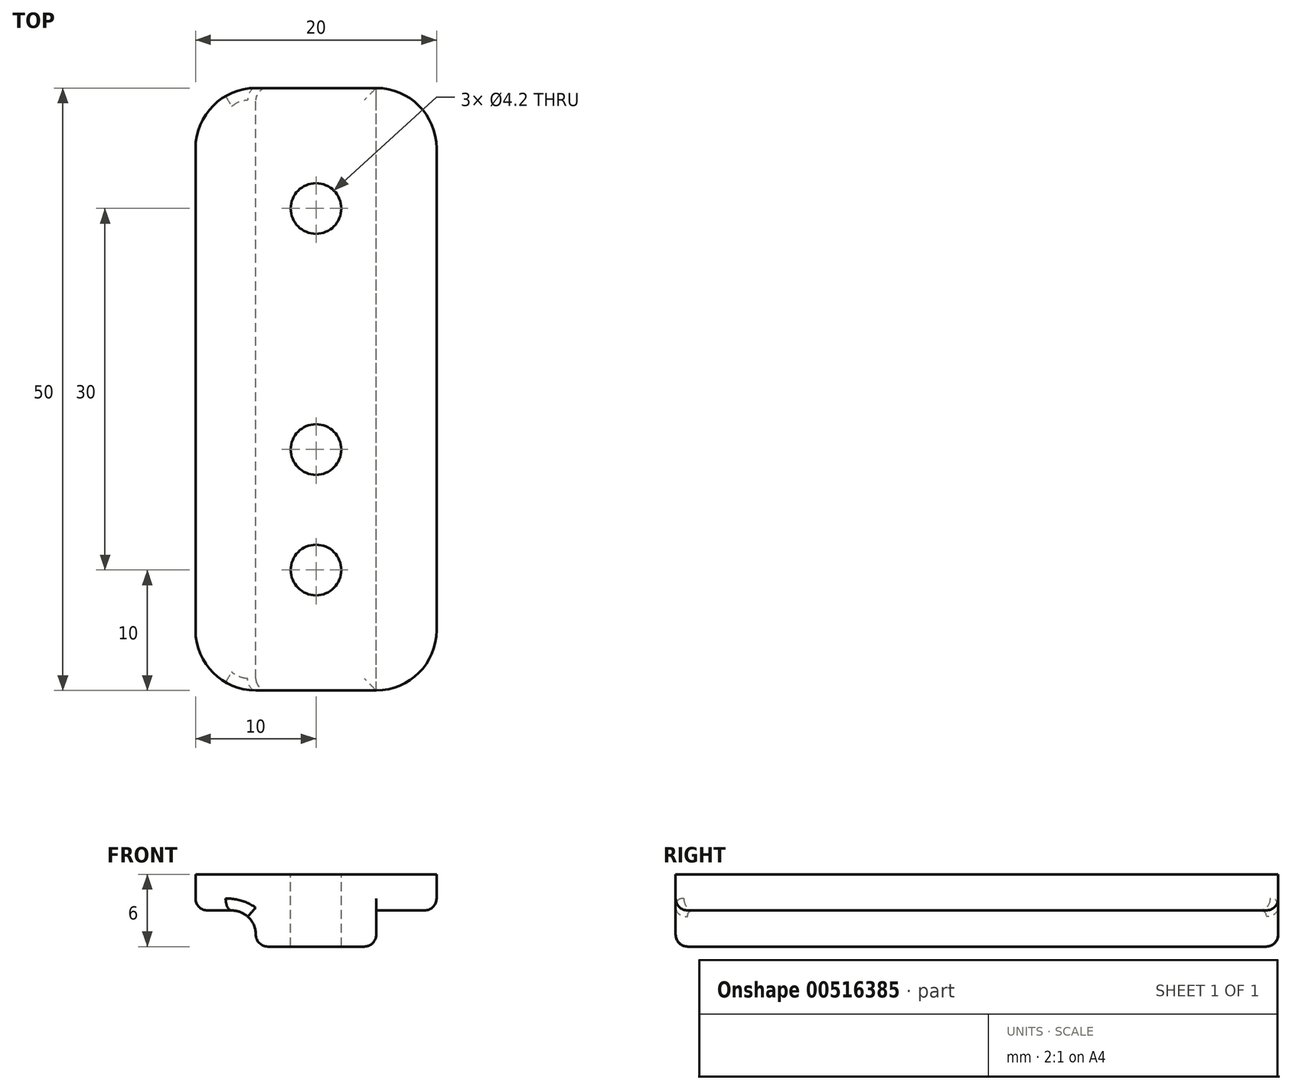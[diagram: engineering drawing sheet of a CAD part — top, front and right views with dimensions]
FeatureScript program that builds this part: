
annotation { "Feature Type Name" : "Feature", "Feature Type Description" : "" }
export const myFeature = defineFeature(function(context is Context, id is Id, definition is map)
    precondition{}
    {
        {
            var Q0;
            Q0=qCreatedBy(makeId("Top.planeOp"),FACE);
            var sketch = newSketch(context, id + "F0", { "sketchPlane" : qUnion([Q0])});
            skLineSegment(sketch, "E0.bottom", {"start": v(-10, 25) * mm, "end": v(10, 25) * mm});
            skLineSegment(sketch, "E0.top", {"start": v(-10, -25) * mm, "end": v(10, -25) * mm});
            skLineSegment(sketch, "E0.left", {"start": v(-10, 25) * mm, "end": v(-10, -25) * mm});
            skLineSegment(sketch, "E0.right", {"start": v(10, 25) * mm, "end": v(10, -25) * mm});
            skSolve(sketch);
        }
        {
            var Q0;
            Q0 = qSketchRegion(id + "F0", true);
            extrude(context, id + "F1", {"entities" : qUnion([Q0]), "depth" : 3 * mm, "offsetDistance" : 25 * mm});
        }
        {
            var Q0;
            Q0=makeQuery(id+"F1.opExtrude","CAP_FACE",FACE,{"disambiguationData":[OSD([sQuery(id+"F0.wireOp",EDGE,"E0.bottom"),sQuery(id+"F0.wireOp",EDGE,"E0.top"),sQuery(id+"F0.wireOp",EDGE,"E0.left"),sQuery(id+"F0.wireOp",EDGE,"E0.right")])],"isStart":false});
            var sketch = newSketch(context, id + "F2", { "sketchPlane" : qUnion([Q0])});
            skCircle(sketch, "E1", {"center": v(0, 15) * mm, "radius": 2.1 * mm});
            skCircle(sketch, "E2", {"center": v(0, -5) * mm, "radius": 2.1 * mm});
            skCircle(sketch, "E3", {"center": v(0, -15) * mm, "radius": 2.1 * mm});
            skSolve(sketch);
        }
        {
            var Q0;
            Q0 = qSketchRegion(id + "F2", true);
            extrude(context, id + "F3", {"entities" : qUnion([Q0]), "operationType" : NewBodyOperationType.REMOVE, "endBound" : BoundingType.THROUGH_ALL, "oppositeDirection" : true, "depth" : 25 * mm, "offsetDistance" : 25 * mm});
        }
        {
            var Q0;
            Q0=makeQuery(id+"F1.opExtrude","SWEPT_EDGE",EDGE,{"disambiguationData":[OSD([sQuery(id+"F0.wireOp",EDGE,"E0.top"),sQuery(id+"F0.wireOp",EDGE,"E0.right")])]});
            var Q1;
            Q1=makeQuery(id+"F1.opExtrude","SWEPT_EDGE",EDGE,{"disambiguationData":[OSD([sQuery(id+"F0.wireOp",EDGE,"E0.top"),sQuery(id+"F0.wireOp",EDGE,"E0.left")])]});
            var Q2;
            Q2=makeQuery(id+"F1.opExtrude","SWEPT_EDGE",EDGE,{"disambiguationData":[OSD([sQuery(id+"F0.wireOp",EDGE,"E0.bottom"),sQuery(id+"F0.wireOp",EDGE,"E0.right")])]});
            var Q3;
            Q3=makeQuery(id+"F1.opExtrude","SWEPT_EDGE",EDGE,{"disambiguationData":[OSD([sQuery(id+"F0.wireOp",EDGE,"E0.bottom"),sQuery(id+"F0.wireOp",EDGE,"E0.left")])]});
            fillet(context, id + "F4", {"entities" : qUnion([Q0, Q1, Q2, Q3]), "radius" : 5 * mm, "tangentPropagation" : true, "allowEdgeOverflow" : false});
        }
        {
            var Q0;
            Q0=makeQuery(id+"F1.opExtrude","CAP_FACE",FACE,{"disambiguationData":[OSD([sQuery(id+"F0.wireOp",EDGE,"E0.bottom"),sQuery(id+"F0.wireOp",EDGE,"E0.top"),sQuery(id+"F0.wireOp",EDGE,"E0.left"),sQuery(id+"F0.wireOp",EDGE,"E0.right")])],"isStart":true});
            var sketch = newSketch(context, id + "F5", { "sketchPlane" : qUnion([Q0])});
            skLineSegment(sketch, "E4.bottom", {"start": v(-5, 25) * mm, "end": v(5, 25) * mm});
            skLineSegment(sketch, "E4.top", {"start": v(-5, -25) * mm, "end": v(5, -25) * mm});
            skLineSegment(sketch, "E4.left", {"start": v(-5, 25) * mm, "end": v(-5, -25) * mm});
            skLineSegment(sketch, "E4.right", {"start": v(5, 25) * mm, "end": v(5, -25) * mm});
            skSolve(sketch);
        }
        {
            var Q0;
            Q0=makeQuery(id+"F5.imprint","IMPRINT",FACE,{"disambiguationData":[TD([[makeQuery(id+"F5.imprint","IMPRINT",EDGE,{"derivedFrom":sQuery(id+"F5.wireOp",EDGE,"E4.bottom")}),-1.0]])]});
            extrude(context, id + "F6", {"entities" : qUnion([Q0]), "operationType" : NewBodyOperationType.ADD, "depth" : 3 * mm, "offsetDistance" : 25 * mm});
        }
        {
            var Q0;
            Q0=makeQuery(id+"F6.opExtrude","CAP_EDGE",EDGE,{"disambiguationData":[OSD([sQuery(id+"F5.wireOp",EDGE,"E4.left")])],"isStart":true});
            var Q1;
            Q1=makeQuery(id+"F6.opExtrude","CAP_EDGE",EDGE,{"disambiguationData":[OSD([sQuery(id+"F5.wireOp",EDGE,"E4.right")])],"isStart":true});
            fillet(context, id + "F7", {"entities" : qUnion([Q0, Q1]), "radius" : 2 * mm, "tangentPropagation" : true, "allowEdgeOverflow" : false});
        }
        {
            var Q0;
            Q0=makeQuery(id+"F6.opExtrude","CAP_EDGE",EDGE,{"disambiguationData":[OSD([sQuery(id+"F5.wireOp",EDGE,"E4.left")])],"isStart":false});
            var Q1;
            Q1=makeQuery(id+"F6.opExtrude","CAP_EDGE",EDGE,{"disambiguationData":[OSD([sQuery(id+"F5.wireOp",EDGE,"E4.right")])],"isStart":false});
            var Q2;
            Q2=makeQuery(id+"F6.opExtrude","CAP_EDGE",EDGE,{"disambiguationData":[OSD([sQuery(id+"F5.wireOp",EDGE,"E4.top")])],"isStart":false});
            var Q3;
            Q3=makeQuery(id+"F6.opExtrude","CAP_EDGE",EDGE,{"disambiguationData":[OSD([sQuery(id+"F5.wireOp",EDGE,"E4.bottom")])],"isStart":false});
            fillet(context, id + "F8", {"entities" : qUnion([Q0, Q1, Q2, Q3]), "radius" : 1 * mm, "tangentPropagation" : true, "allowEdgeOverflow" : false});
        }
        {
            var Q0;
            {var subQ0=sQuery(id+"F0.wireOp",EDGE,"E0.left");var subQ1=sQuery(id+"F0.wireOp",EDGE,"E0.bottom");Q0=makeQuery(id+"F4.opFillet","BLEND_EDGE",EDGE,{"blendedFrom":[makeQuery(id+"F1.opExtrude","SWEPT_EDGE",EDGE,{"disambiguationData":[OSD([subQ1,subQ0])]}),makeQuery(id+"F1.opExtrude","CAP_FACE",FACE,{"disambiguationData":[OSD([subQ1,sQuery(id+"F0.wireOp",EDGE,"E0.top"),subQ0,sQuery(id+"F0.wireOp",EDGE,"E0.right")])],"isStart":true})],"blendedInto":[makeQuery(id+"F1.opExtrude","CAP_FACE",FACE,{"disambiguationData":[OSD([subQ1,sQuery(id+"F0.wireOp",EDGE,"E0.top"),subQ0,sQuery(id+"F0.wireOp",EDGE,"E0.right")])],"isStart":true})]});}
            var Q1;
            {var subQ0=sQuery(id+"F0.wireOp",EDGE,"E0.right");var subQ1=sQuery(id+"F0.wireOp",EDGE,"E0.bottom");Q1=makeQuery(id+"F4.opFillet","BLEND_EDGE",EDGE,{"blendedFrom":[makeQuery(id+"F1.opExtrude","SWEPT_EDGE",EDGE,{"disambiguationData":[OSD([subQ1,subQ0])]}),makeQuery(id+"F1.opExtrude","CAP_FACE",FACE,{"disambiguationData":[OSD([subQ1,sQuery(id+"F0.wireOp",EDGE,"E0.top"),sQuery(id+"F0.wireOp",EDGE,"E0.left"),subQ0])],"isStart":true})],"blendedInto":[makeQuery(id+"F1.opExtrude","CAP_FACE",FACE,{"disambiguationData":[OSD([subQ1,sQuery(id+"F0.wireOp",EDGE,"E0.top"),sQuery(id+"F0.wireOp",EDGE,"E0.left"),subQ0])],"isStart":true})]});}
            fillet(context, id + "F9", {"entities" : qUnion([Q0, Q1]), "radius" : 1 * mm, "tangentPropagation" : true, "allowEdgeOverflow" : false});
        }
    });
